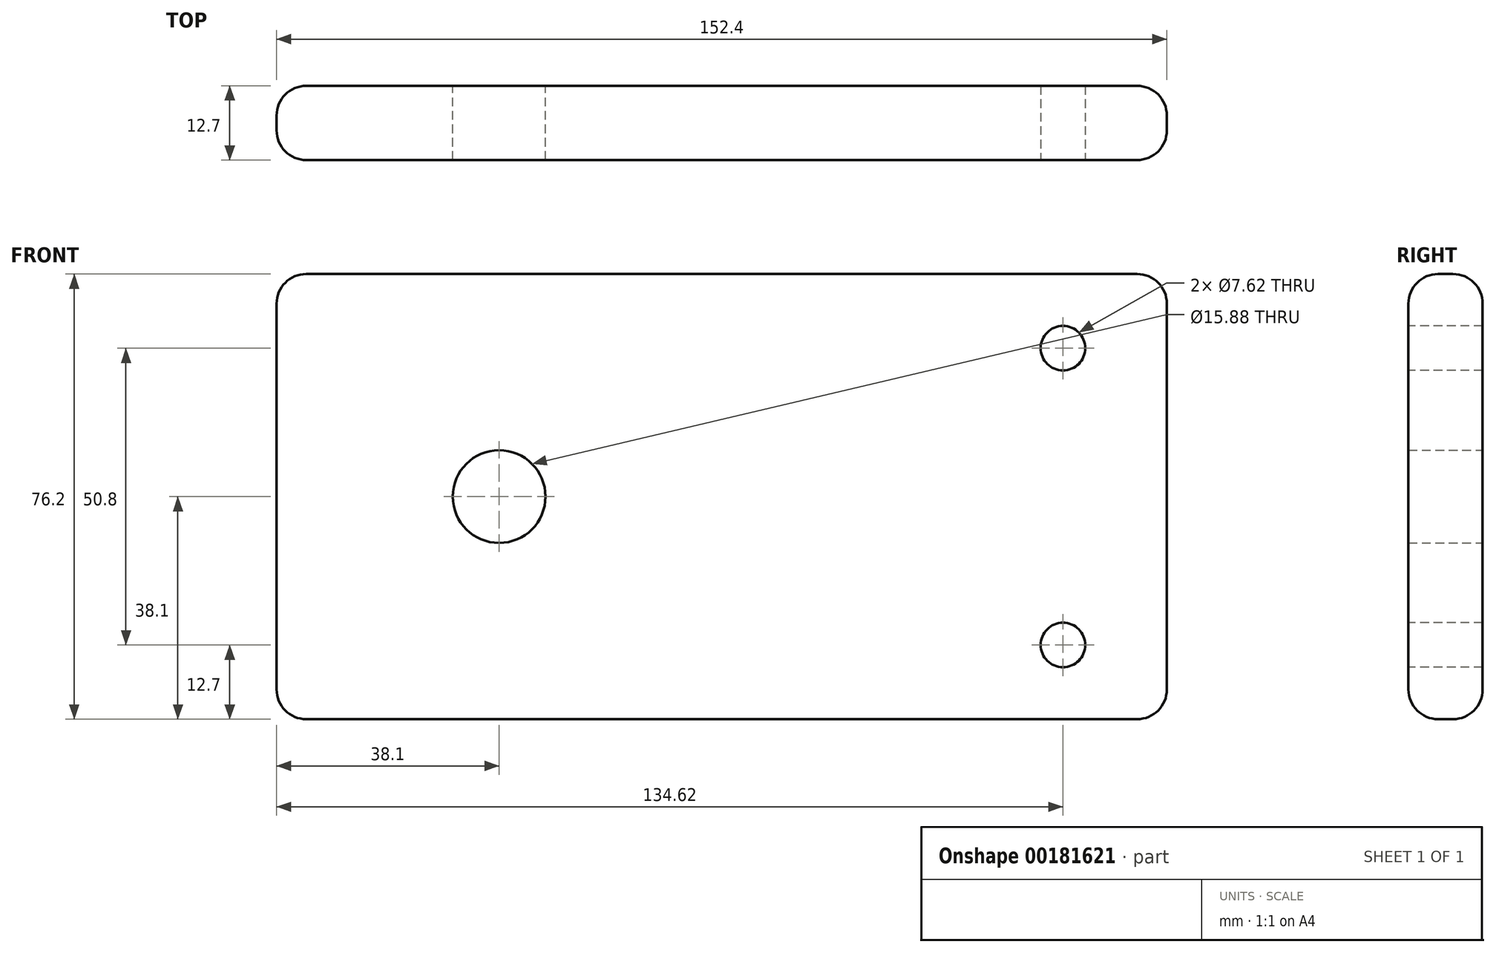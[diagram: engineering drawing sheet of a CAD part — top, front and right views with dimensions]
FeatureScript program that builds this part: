
annotation { "Feature Type Name" : "Feature", "Feature Type Description" : "" }
export const myFeature = defineFeature(function(context is Context, id is Id, definition is map)
    precondition{}
    {
        {
            var Q0;
            Q0=qCreatedBy(makeId("Front.planeOp"),FACE);
            var sketch = newSketch(context, id + "F0", { "sketchPlane" : qUnion([Q0])});
            skLineSegment(sketch, "E0.bottom", {"start": v(76.2, -38.1) * mm, "end": v(-76.2, -38.1) * mm});
            skLineSegment(sketch, "E0.top", {"start": v(76.2, 38.1) * mm, "end": v(-76.2, 38.1) * mm});
            skLineSegment(sketch, "E0.left", {"start": v(76.2, -38.1) * mm, "end": v(76.2, 38.1) * mm});
            skLineSegment(sketch, "E0.right", {"start": v(-76.2, -38.1) * mm, "end": v(-76.2, 38.1) * mm});
            skPoint(sketch, "E0.middle", {"position": v(0, 0) * mm});
            skPoint(sketch, "E1.orphan", {"position": v(0, 38.1) * mm});
            skPoint(sketch, "E2.orphan", {"position": v(-76.2, 0) * mm});
            skPoint(sketch, "E3.end.orphan", {"position": v(76.2, 0) * mm});
            skPoint(sketch, "E4.start.orphan", {"position": v(0, -38.1) * mm});
            skCircle(sketch, "E5", {"center": v(-38.1, 0) * mm, "radius": 7.94 * mm});
            skSolve(sketch);
        }
        {
            var Q0;
            Q0 = qSketchRegion(id + "F0", true);
            extrude(context, id + "F1", {"entities" : qUnion([Q0]), "endBound" : BoundingType.SYMMETRIC, "depth" : 12.7 * mm});
        }
        {
            var Q0;
            Q0=makeQuery(id+"F1.opExtrude","CAP_EDGE",EDGE,{"disambiguationData":[OSD([sQuery(id+"F0.wireOp",EDGE,"E0.top")])],"isStart":false});
            var Q1;
            Q1=makeQuery(id+"F1.opExtrude","CAP_EDGE",EDGE,{"disambiguationData":[OSD([sQuery(id+"F0.wireOp",EDGE,"E0.right")])],"isStart":false});
            var Q2;
            Q2=makeQuery(id+"F1.opExtrude","CAP_EDGE",EDGE,{"disambiguationData":[OSD([sQuery(id+"F0.wireOp",EDGE,"E0.bottom")])],"isStart":false});
            var Q3;
            Q3=makeQuery(id+"F1.opExtrude","CAP_EDGE",EDGE,{"disambiguationData":[OSD([sQuery(id+"F0.wireOp",EDGE,"E0.left")])],"isStart":false});
            var Q4;
            Q4=makeQuery(id+"F1.opExtrude","CAP_EDGE",EDGE,{"disambiguationData":[OSD([sQuery(id+"F0.wireOp",EDGE,"E0.right")])],"isStart":true});
            var Q5;
            Q5=makeQuery(id+"F1.opExtrude","SWEPT_EDGE",EDGE,{"disambiguationData":[OSD([sQuery(id+"F0.wireOp",EDGE,"E0.bottom"),sQuery(id+"F0.wireOp",EDGE,"E0.right")])]});
            var Q6;
            Q6=makeQuery(id+"F1.opExtrude","CAP_EDGE",EDGE,{"disambiguationData":[OSD([sQuery(id+"F0.wireOp",EDGE,"E0.bottom")])],"isStart":true});
            var Q7;
            Q7=makeQuery(id+"F1.opExtrude","CAP_EDGE",EDGE,{"disambiguationData":[OSD([sQuery(id+"F0.wireOp",EDGE,"E0.left")])],"isStart":true});
            var Q8;
            Q8=makeQuery(id+"F1.opExtrude","SWEPT_EDGE",EDGE,{"disambiguationData":[OSD([sQuery(id+"F0.wireOp",EDGE,"E0.bottom"),sQuery(id+"F0.wireOp",EDGE,"E0.left")])]});
            var Q9;
            Q9=makeQuery(id+"F1.opExtrude","SWEPT_EDGE",EDGE,{"disambiguationData":[OSD([sQuery(id+"F0.wireOp",EDGE,"E0.top"),sQuery(id+"F0.wireOp",EDGE,"E0.left")])]});
            var Q10;
            Q10=makeQuery(id+"F1.opExtrude","CAP_EDGE",EDGE,{"disambiguationData":[OSD([sQuery(id+"F0.wireOp",EDGE,"E0.top")])],"isStart":true});
            fillet(context, id + "F2", {"entities" : qUnion([Q0, Q1, Q2, Q3, Q4, Q5, Q6, Q7, Q8, Q9, Q10]), "radius" : 5.08 * mm, "tangentPropagation" : true, "allowEdgeOverflow" : false});
        }
        {
            var Q0;
            Q0=makeQuery(id+"F1.opExtrude","SWEPT_EDGE",EDGE,{"disambiguationData":[OSD([sQuery(id+"F0.wireOp",EDGE,"E0.top"),sQuery(id+"F0.wireOp",EDGE,"E0.right")])]});
            fillet(context, id + "F3", {"entities" : qUnion([Q0]), "radius" : 5.08 * mm, "tangentPropagation" : true, "allowEdgeOverflow" : false});
        }
        {
            var Q0;
            Q0=makeQuery(id+"F1.opExtrude","CAP_FACE",FACE,{"disambiguationData":[OSD([sQuery(id+"F0.wireOp",EDGE,"E0.bottom"),sQuery(id+"F0.wireOp",EDGE,"E0.top"),sQuery(id+"F0.wireOp",EDGE,"E0.left"),sQuery(id+"F0.wireOp",EDGE,"E0.right"),sQuery(id+"F0.wireOp",EDGE,"Es5Al8rZ-qbiS-vJD7-UXtx-vFfOWRUnKKIw")])],"isStart":false});
            var sketch = newSketch(context, id + "F4", { "sketchPlane" : qUnion([Q0])});
            skPoint(sketch, "E6.start.orphan", {"position": v(0, 0) * mm});
            skPoint(sketch, "E7.trimOffspring.end.orphan", {"position": v(71.12, 0) * mm});
            skPoint(sketch, "E8.trimOffspring.end.orphan", {"position": v(-71.12, 0) * mm});
            skCircle(sketch, "E9", {"center": v(58.42, 25.4) * mm, "radius": 3.81 * mm});
            skCircle(sketch, "E10", {"center": v(58.42, -25.4) * mm, "radius": 3.81 * mm});
            skSolve(sketch);
        }
        {
            var Q0;
            Q0 = qSketchRegion(id + "F4", true);
            extrude(context, id + "F5", {"entities" : qUnion([Q0]), "operationType" : NewBodyOperationType.REMOVE, "oppositeDirection" : true, "depth" : 25.4 * mm});
        }
    });
